FCSTD DOCUMENT  (FreeCAD 0.19R24276 (Git))
Label: heatsink
License: Creative Commons Attribution-NonCommercial-ShareAlike
LicenseURL: http://creativecommons.org/licenses/by-nc-sa/4.0/
objects: PartDesign::Body×1, Image::ImagePlane×1, Sketcher::SketchObject×1, PartDesign::Pad×1, PartDesign::CoordinateSystem×1, App::Part×1
note: 5 computed .brp shape members not serialized (recipe doc carries the construction recipe); baked Part::Feature solids carry a one-line shape summary decoded from their .brp

FEATURE [PartDesign::Body] Body
  Origin = -> Origin
FEATURE [Image::ImagePlane] ImagePlane
  Placement = pos=(0,0,-0.0001) rot=(0,0,1;0rad)
  XSize = 189.664
  YSize = 135.264
FEATURE [Sketcher::SketchObject] Sketch002  label="heatsink"
  FullyConstrained = true
  sketch-geometry (66):
    g0: LineSegment StartX=64.9692 StartY=-39.4035 StartZ=0 EndX=64.9692 EndY=-33.0535 EndZ=0
    g1: LineSegment StartX=64.9692 StartY=-33.0535 StartZ=0 EndX=61.9692 EndY=-33.0535 EndZ=0
    g2: LineSegment StartX=61.9692 StartY=-33.0535 StartZ=0 EndX=61.9692 EndY=-34.5535 EndZ=0
    g3: LineSegment StartX=61.9692 StartY=-34.5535 StartZ=0 EndX=56.9692 EndY=-34.5535 EndZ=0
    g4: LineSegment StartX=56.9692 StartY=-26.2535 StartZ=0 EndX=61.9692 EndY=-26.2535 EndZ=0
    g5: LineSegment StartX=61.9692 StartY=-26.2535 StartZ=0 EndX=61.9692 EndY=-27.7535 EndZ=0
    g6: LineSegment StartX=61.9692 StartY=-27.7535 StartZ=0 EndX=64.9692 EndY=-27.7535 EndZ=0
    g7: LineSegment StartX=64.9692 StartY=-27.7535 StartZ=0 EndX=64.9692 EndY=26.5965 EndZ=0
    g8: LineSegment StartX=66.9692 StartY=28.5965 StartZ=0 EndX=77.4692 EndY=28.5965 EndZ=0
    g9: LineSegment StartX=77.4692 StartY=28.5965 StartZ=0 EndX=77.4692 EndY=30.5965 EndZ=0
    g10: LineSegment StartX=77.4692 StartY=30.5965 StartZ=0 EndX=64.9692 EndY=30.5965 EndZ=0
    g11: LineSegment StartX=62.9692 StartY=28.5965 StartZ=0 EndX=62.9692 EndY=-15.4035 EndZ=0
    g12: LineSegment StartX=54.9692 StartY=-15.4035 StartZ=0 EndX=53.1692 EndY=29.3465 EndZ=0
    g13: LineSegment StartX=51.0549 StartY=29.3465 StartZ=0 EndX=50.2549 EndY=-24.4035 EndZ=0
    g14: LineSegment StartX=38.2549 StartY=-24.4035 StartZ=0 EndX=37.4549 EndY=29.3465 EndZ=0
    g15: LineSegment StartX=35.3406 StartY=29.3465 StartZ=0 EndX=34.5406 EndY=-24.4035 EndZ=0
    g16: LineSegment StartX=22.5406 StartY=-24.4035 StartZ=0 EndX=21.7406 EndY=29.3465 EndZ=0
    g17: LineSegment StartX=19.6263 StartY=29.3465 StartZ=0 EndX=18.8263 EndY=-24.4035 EndZ=0
    g18: LineSegment StartX=6.8263 StartY=-24.4035 StartZ=0 EndX=6.0263 EndY=29.3465 EndZ=0
    g19: ArcOfCircle CenterX=28.5406 CenterY=-24.4035 CenterZ=0 NormalX=0 NormalY=0 NormalZ=1 AngleXU=0 Radius=6 StartAngle=3.14159 EndAngle=6.28319
    g20: ArcOfCircle CenterX=12.8263 CenterY=-24.4035 CenterZ=0 NormalX=0 NormalY=0 NormalZ=1 AngleXU=0 Radius=6 StartAngle=3.14159 EndAngle=6.28319
    g21: ArcOfCircle CenterX=44.2549 CenterY=-24.4035 CenterZ=0 NormalX=0 NormalY=0 NormalZ=1 AngleXU=0 Radius=6 StartAngle=3.14159 EndAngle=6.28319
    g22: ArcOfCircle CenterX=58.9692 CenterY=-15.4035 CenterZ=0 NormalX=0 NormalY=0 NormalZ=1 AngleXU=0 Radius=4 StartAngle=3.14159 EndAngle=6.28319
    g23: ArcOfCircle CenterX=52.112 CenterY=29.3465 CenterZ=0 NormalX=0 NormalY=0 NormalZ=1 AngleXU=0 Radius=1.05714 StartAngle=0 EndAngle=3.14159
    g24: ArcOfCircle CenterX=20.6834 CenterY=29.3465 CenterZ=0 NormalX=0 NormalY=0 NormalZ=1 AngleXU=0 Radius=1.05714 StartAngle=0 EndAngle=3.14159
    g25: LineSegment StartX=56.9692 StartY=-26.2535 StartZ=0 EndX=56.9692 EndY=-30.4035 EndZ=0
    g26: LineSegment StartX=56.9692 StartY=-30.4035 StartZ=0 EndX=56.9692 EndY=-34.5535 EndZ=0
    g27: LineSegment StartX=-55.0308 StartY=-39.4035 StartZ=0 EndX=-55.0308 EndY=-33.0535 EndZ=0
    g28: LineSegment StartX=-55.0308 StartY=-33.0535 StartZ=0 EndX=-52.0308 EndY=-33.0535 EndZ=0
    g29: LineSegment StartX=-52.0308 StartY=-33.0535 StartZ=0 EndX=-52.0308 EndY=-34.5535 EndZ=0
    g30: LineSegment StartX=-52.0308 StartY=-34.5535 StartZ=0 EndX=-47.0308 EndY=-34.5535 EndZ=0
    g31: LineSegment StartX=-47.0308 StartY=-26.2535 StartZ=0 EndX=-52.0308 EndY=-26.2535 EndZ=0
    g32: LineSegment StartX=-52.0308 StartY=-26.2535 StartZ=0 EndX=-52.0308 EndY=-27.7535 EndZ=0
    g33: LineSegment StartX=-52.0308 StartY=-27.7535 StartZ=0 EndX=-55.0308 EndY=-27.7535 EndZ=0
    g34: LineSegment StartX=-55.0308 StartY=-27.7535 StartZ=0 EndX=-55.0308 EndY=26.5965 EndZ=0
    g35: LineSegment StartX=-57.0308 StartY=28.5965 StartZ=0 EndX=-67.5308 EndY=28.5965 EndZ=0
    g36: LineSegment StartX=-67.5308 StartY=28.5965 StartZ=0 EndX=-67.5308 EndY=30.5965 EndZ=0
    g37: LineSegment StartX=-67.5308 StartY=30.5965 StartZ=0 EndX=-55.0308 EndY=30.5965 EndZ=0
    g38: LineSegment StartX=-53.0308 StartY=28.5965 StartZ=0 EndX=-53.0308 EndY=-15.4035 EndZ=0
    g39: LineSegment StartX=-45.0308 StartY=-15.4035 StartZ=0 EndX=-43.2308 EndY=29.3465 EndZ=0
    g40: LineSegment StartX=-41.1166 StartY=29.3465 StartZ=0 EndX=-40.3166 EndY=-24.4035 EndZ=0
    g41: LineSegment StartX=-28.3166 StartY=-24.4035 StartZ=0 EndX=-27.5166 EndY=29.3465 EndZ=0
    g42: LineSegment StartX=-25.4023 StartY=29.3465 StartZ=0 EndX=-24.6023 EndY=-24.4035 EndZ=0
    g43: LineSegment StartX=-12.6023 StartY=-24.4035 StartZ=0 EndX=-11.8023 EndY=29.3465 EndZ=0
    g44: LineSegment StartX=-9.68798 StartY=29.3465 StartZ=0 EndX=-8.88798 EndY=-24.4035 EndZ=0
    g45: LineSegment StartX=3.11202 StartY=-24.4035 StartZ=0 EndX=3.91202 EndY=29.3465 EndZ=0
    g46: ArcOfCircle CenterX=-18.6023 CenterY=-24.4035 CenterZ=0 NormalX=0 NormalY=0 NormalZ=1 AngleXU=0 Radius=6 StartAngle=3.14159 EndAngle=6.28319
    g47: ArcOfCircle CenterX=-2.88798 CenterY=-24.4035 CenterZ=0 NormalX=0 NormalY=0 NormalZ=1 AngleXU=0 Radius=6 StartAngle=3.14159 EndAngle=6.28319
    g48: ArcOfCircle CenterX=-34.3166 CenterY=-24.4035 CenterZ=0 NormalX=0 NormalY=0 NormalZ=1 AngleXU=0 Radius=6 StartAngle=3.14159 EndAngle=6.28319
    g49: ArcOfCircle CenterX=-49.0308 CenterY=-15.4035 CenterZ=0 NormalX=0 NormalY=0 NormalZ=1 AngleXU=0 Radius=4 StartAngle=3.14159 EndAngle=6.28319
    g50: ArcOfCircle CenterX=-42.1737 CenterY=29.3465 CenterZ=0 NormalX=0 NormalY=0 NormalZ=1 AngleXU=0 Radius=1.05714 StartAngle=0 EndAngle=3.14159
    g51: ArcOfCircle CenterX=-26.4594 CenterY=29.3465 CenterZ=0 NormalX=0 NormalY=0 NormalZ=1 AngleXU=0 Radius=1.05714 StartAngle=3e-16 EndAngle=3.14159
    g52: ArcOfCircle CenterX=-10.7451 CenterY=29.3465 CenterZ=0 NormalX=0 NormalY=0 NormalZ=1 AngleXU=0 Radius=1.05714 StartAngle=6e-16 EndAngle=3.14159
    g53: ArcOfCircle CenterX=4.96916 CenterY=29.3465 CenterZ=0 NormalX=0 NormalY=0 NormalZ=1 AngleXU=0 Radius=1.05714 StartAngle=-9e-16 EndAngle=3.14159
    g54: LineSegment StartX=-47.0308 StartY=-26.2535 StartZ=0 EndX=-47.0308 EndY=-30.4035 EndZ=0
    g55: LineSegment StartX=-47.0308 StartY=-30.4035 StartZ=0 EndX=-47.0308 EndY=-34.5535 EndZ=0
    g56: ArcOfCircle CenterX=36.3977 CenterY=29.3465 CenterZ=0 NormalX=0 NormalY=0 NormalZ=1 AngleXU=0 Radius=1.05714 StartAngle=-9e-16 EndAngle=3.14159
    g57: ArcOfCircle CenterX=-57.0308 CenterY=26.5965 CenterZ=0 NormalX=0 NormalY=0 NormalZ=1 AngleXU=0 Radius=2 StartAngle=0 EndAngle=1.5708
    g58: GeomPoint X=-55.0308 Y=28.5965 Z=0
    g59: ArcOfCircle CenterX=-55.0308 CenterY=28.5965 CenterZ=0 NormalX=0 NormalY=0 NormalZ=1 AngleXU=0 Radius=2 StartAngle=0 EndAngle=1.5708
    g60: GeomPoint X=-53.0308 Y=30.5965 Z=0
    g61: ArcOfCircle CenterX=66.9692 CenterY=26.5965 CenterZ=0 NormalX=0 NormalY=0 NormalZ=1 AngleXU=0 Radius=2 StartAngle=1.5708 EndAngle=3.14159
    g62: GeomPoint X=64.9692 Y=28.5965 Z=0
    g63: ArcOfCircle CenterX=64.9692 CenterY=28.5965 CenterZ=0 NormalX=0 NormalY=0 NormalZ=1 AngleXU=0 Radius=2 StartAngle=1.5708 EndAngle=3.14159
    g64: GeomPoint X=62.9692 Y=30.5965 Z=0
    g65: LineSegment StartX=64.9692 StartY=-39.4035 StartZ=0 EndX=-55.0308 EndY=-39.4035 EndZ=0
  constraints (209):
    c: Horizontal(g8)
    c: Horizontal(g10)
    c: Radius(g22) = 4
    c: Radius(g21) = 6
    c: Equal(g21,g19)
    c: Equal(g21,g20)
    c: Vertical(g9)
    c: Vertical(g7)
    c: Vertical(g0)
    c: Vertical(g5)
    c: Vertical(g2)
    c: Horizontal(g6)
    c: Horizontal(g1)
    c: Horizontal(g3)
    c: Horizontal(g4)
    c: Coincident(g13,g23)
    c: Coincident(g12,g23)
    c: Coincident(g24,g16)
    c: Coincident(g24,g17)
    c: Equal(g23,g24)
    c: Equal(g6,g1)
    c: Equal(g5,g2)
    c: Equal(g4,g3)
    c: Distance(g6,g0) = 5.3
    c: Coincident(g4,g5)
    c: Coincident(g2,g3)
    c: Coincident(g1,g2)
    c: Coincident(g0,g1)
    c: Coincident(g6,g7)
    c: Coincident(g9,g10)
    c: Coincident(g8,g9)
    c: Vertical(g11)
    c: Coincident(g5,g6)
    c: Coincident(g13,g21)
    c: Coincident(g14,g21)
    c: Coincident(g15,g19)
    c: Coincident(g16,g19)
    c: Coincident(g17,g20)
    c: Coincident(g18,g20)
    c: Coincident(g12,g22)
    c: Coincident(g11,g22)
    c: Coincident(g25,g4)
    c: Vertical(g25)
    c: Coincident(g26,g25)
    c: Coincident(g26,g3)
    c: Vertical(g26)
    c: Equal(g26,g25)
    c: Horizontal(g35)
    c: Horizontal(g37)
    c: Radius(g49) = 4
    c: Radius(g48) = 6
    c: Equal(g48,g46)
    c: Equal(g48,g47)
    c: Vertical(g36)
    c: Vertical(g34)
    c: Vertical(g27)
    c: Vertical(g32)
    c: Vertical(g29)
    c: Horizontal(g33)
    c: Horizontal(g28)
    c: Horizontal(g30)
    c: Horizontal(g31)
    c: Coincident(g40,g50)
    c: Coincident(g39,g50)
    c: Coincident(g51,g42)
    c: Coincident(g52,g43)
    c: Coincident(g52,g44)
    c: Coincident(g53,g45)
    c: Equal(g50,g52)
    c: Equal(g33,g28)
    c: Equal(g32,g29)
    c: Equal(g31,g30)
    c: Distance(g33,g27) = 5.3
    c: DistanceY(g30,g31) = 8.3
    c: Coincident(g31,g32)
    c: Coincident(g29,g30)
    c: Coincident(g28,g29)
    c: Coincident(g27,g28)
    c: Coincident(g33,g34)
    c: Coincident(g36,g37)
    c: Coincident(g35,g36)
    c: Vertical(g38)
    c: DistanceX(g60,g39) = 9.8
    c: DistanceX(g36,g60) = 14.5
    c: DistanceY(g27,g36) = 70
    c: Coincident(g32,g33)
    c: Coincident(g40,g48)
    c: Coincident(g41,g48)
    c: Coincident(g42,g46)
    c: Coincident(g43,g46)
    c: Coincident(g44,g47)
    c: Coincident(g45,g47)
    c: Coincident(g39,g49)
    c: Coincident(g38,g49)
    c: DistanceY(g38,g39) = 0
    c: DistanceY(g41,g40) = 0
    c: DistanceY(g42,g43) = 0
    c: DistanceY(g44,g45) = 0
    c: DistanceY(g41,g42) = 0
    c: DistanceY(g43,g44) = 0
    c: Coincident(g54,g31)
    c: Vertical(g54)
    c: Coincident(g55,g54)
    c: Coincident(g55,g30)
    c: Vertical(g55)
    c: Equal(g55,g54)
    c: DistanceX(g28,g28) = 3
    c: DistanceX(g30,g30) = 5
    c: DistanceX(g27) = -55.0308
    c: DistanceY(g27) = -39.4035
    c: DistanceY(g40,g39) = 0
    c: DistanceY(g41,g42) = 0
    c: DistanceY(g43,g44) = 0
    c: DistanceY(g53,g45) = 0
    c: DistanceY(g40,g50) = 0
    c: DistanceY(g41,g51) = 0
    c: DistanceY(g52,g43) = 0
    c: DistanceY(g45,g53) = 0
    c: DistanceY(g39,g60) = 1.25
    c: DistanceY(g50,g51) = 0
    c: DistanceY(g52,g53) = 0
    c: DistanceY(g36,g36) = 2
    c: DistanceY(g51,g52) = 0
    c: Equal(g4,g31)
    c: Equal(g25,g54)
    c: Equal(g33,g6)
    c: Equal(g27,g0)
    c: Coincident(g53,g18)
    c: Equal(g9,g36)
    c: DistanceY(g17,g24) = 0
    c: DistanceY(g16,g24) = 0
    c: DistanceY(g53,g24) = 0
    c: DistanceY(g13,g23) = 0
    c: DistanceY(g23,g12) = 0
    c: Coincident(g56,g15)
    c: Coincident(g56,g14)
    c: DistanceY(g56,g15) = 0
    c: DistanceY(g56,g14) = 0
    c: DistanceY(g24,g56) = 0
    c: DistanceY(g56,g23) = 0
    c: DistanceY(g14,g21) = 0
    c: DistanceY(g15,g19) = 0
    c: DistanceY(g16,g19) = 0
    c: DistanceY(g17,g20) = 0
    c: DistanceY(g20,g18) = 0
    c: Parallel(g40,g42)
    c: Parallel(g42,g44)
    c: Parallel(g44,g18)
    c: Parallel(g18,g16)
    c: Parallel(g16,g14)
    c: Parallel(g13,g15)
    c: Parallel(g15,g17)
    c: Parallel(g17,g45)
    c: Parallel(g45,g43)
    c: Parallel(g43,g41)
    c: DistanceX(g12,g64) = 9.8
    c: DistanceY(g12,g22) = 0
    c: DistanceY(g22,g11) = 0
    c: DistanceY(g49,g22) = 0
    c: DistanceX(g44,g45) = 13.6
    c: Equal(g50,g23)
    c: DistanceX(g58,g60) = 2
    c: DistanceX(g64,g62) = 2
    c: Equal(g53,g24)
    c: Equal(g24,g56)
    c: Equal(g18,g45)
    c: DistanceX(g18,g17) = 13.6
    c: Radius(g52) = 1.05714
    c: DistanceX(g27,g0) = 120
    c: Coincident(g41,g51)
    c: PointOnObject(g58,g34)
    c: PointOnObject(g58,g35)
    c: Tangent(g34,g57) = -1.5708
    c: Tangent(g35,g57) = -1.5708
    c: PointOnObject(g60,g37)
    c: PointOnObject(g60,g38)
    c: Tangent(g37,g59) = 1.5708
    c: Tangent(g38,g59) = 1.5708
    c: Radius(g57) = 2
    c: Radius(g59) = 2
    c: PointOnObject(g62,g7)
    c: PointOnObject(g62,g8)
    c: Tangent(g7,g61) = 1.5708
    c: Tangent(g8,g61) = 1.5708
    c: PointOnObject(g64,g10)
    c: PointOnObject(g64,g11)
    c: Tangent(g10,g63) = -1.5708
    c: Tangent(g11,g63) = -1.5708
    c: Radius(g61) = 2
    c: Radius(g63) = 2
    c: Equal(g7,g34)
    c: Equal(g11,g38)
    c: DistanceY(g23,g64) = 1.25
    c: Equal(g10,g37)
    c: Equal(g8,g35)
    c: Coincident(g65,g0)
    c: Coincident(g65,g27)
    c: Horizontal(g65)
    c: Distance(g54,g65) = 9
    c: Distance(g48,g65) = 15
    c: Distance(g46,g65) = 15
    c: Distance(g47,g65) = 15
    c: Distance(g20,g65) = 15
    c: Distance(g19,g65) = 15
    c: Distance(g21,g65) = 15
    c: DistanceY(g18,g45) = 0
    c: DistanceY(g13,g21) = 0
    c: Distance(g49,g65) = 24
    c: Equal(g51,g50)
FEATURE [PartDesign::Pad] Pad
  Direction = (1,1,1)
  Length = 100
  Length2 = 100
  Profile = -> Sketch002
  Type = 0
FEATURE [PartDesign::CoordinateSystem] LCS_1  label="LCS_0"
  AttacherType = Attacher::AttachEngine3D
  AttachmentOffset = pos=(0,0,0) rot=(0.57735,0.57735,0.57735;2.0944rad)
  MapMode = 6
  Placement = pos=(-55.0308,-39.4035,0) rot=(0.707107,0,0.707107;3.14159rad)
  Support = -> [Pad]
FEATURE [App::Part] Part
  Group = -> [Body,Sketch002,Pad,LCS_1]
  Origin = -> Origin001
